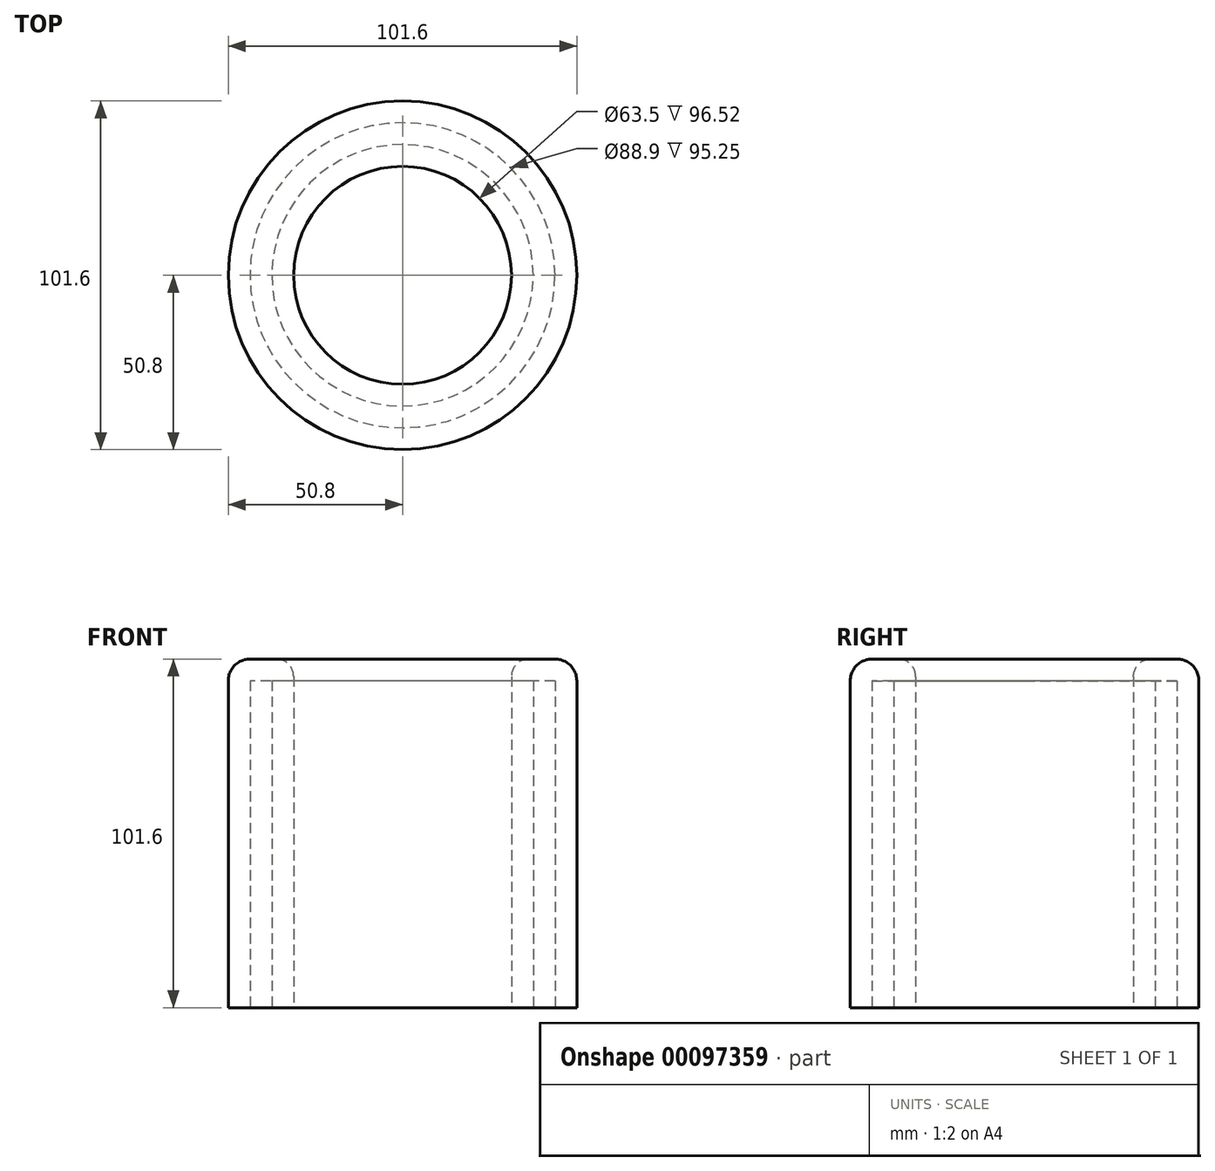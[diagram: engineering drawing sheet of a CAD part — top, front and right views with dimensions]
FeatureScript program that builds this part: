
annotation { "Feature Type Name" : "Feature", "Feature Type Description" : "" }
export const myFeature = defineFeature(function(context is Context, id is Id, definition is map)
    precondition{}
    {
        {
            var Q0;
            Q0=qCreatedBy(makeId("Top.planeOp"),FACE);
            var sketch = newSketch(context, id + "F0", { "sketchPlane" : qUnion([Q0])});
            skCircle(sketch, "E0", {"center": v(0, 0) * mm, "radius": 31.75 * mm});
            skCircle(sketch, "E1", {"center": v(0, 0) * mm, "radius": 50.8 * mm});
            skSolve(sketch);
        }
        {
            var Q0;
            Q0=makeQuery(id+"F0.imprint","IMPRINT",FACE,{"disambiguationData":[TD([[makeQuery(id+"F0.imprint","IMPRINT",EDGE,{"derivedFrom":sQuery(id+"F0.wireOp",EDGE,"E0")}),-1.0]])]});
            extrude(context, id + "F1", {"entities" : qUnion([Q0]), "depth" : 101.6 * mm});
        }
        {
            var Q0;
            Q0=makeQuery(id+"F1.opExtrude","CAP_EDGE",EDGE,{"disambiguationData":[OSD([sQuery(id+"F0.wireOp",EDGE,"E1")])],"isStart":false});
            fillet(context, id + "F2", {"entities" : qUnion([Q0]), "radius" : 6.35 * mm, "tangentPropagation" : true, "allowEdgeOverflow" : false});
        }
        {
            var Q0;
            Q0=makeQuery(id+"F1.opExtrude","CAP_EDGE",EDGE,{"disambiguationData":[OSD([sQuery(id+"F0.wireOp",EDGE,"E0")])],"isStart":false});
            fillet(context, id + "F3", {"entities" : qUnion([Q0]), "radius" : 5.08 * mm, "tangentPropagation" : true, "allowEdgeOverflow" : false});
        }
        {
            var Q0;
            Q0=makeQuery(id+"F1.opExtrude","CAP_FACE",FACE,{"disambiguationData":[OSD([sQuery(id+"F0.wireOp",EDGE,"E0"),sQuery(id+"F0.wireOp",EDGE,"E1")])],"isStart":true});
            shell(context, id + "F4", {"entities" : qUnion([Q0]), "thickness" : 6.35 * mm});
        }
    });
